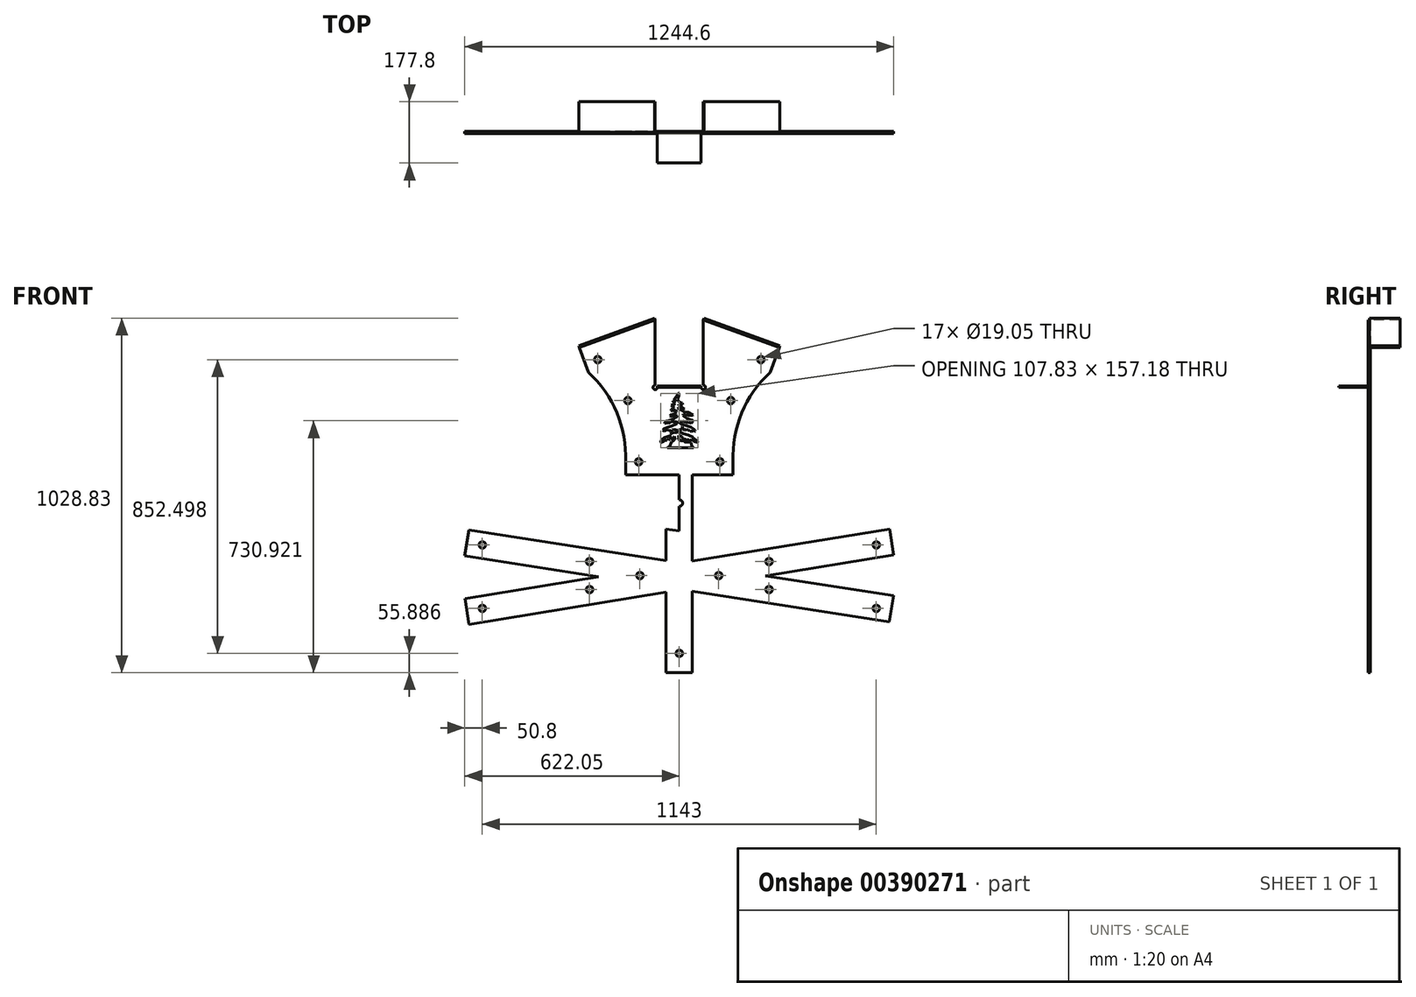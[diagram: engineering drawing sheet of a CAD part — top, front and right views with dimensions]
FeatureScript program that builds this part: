
annotation { "Feature Type Name" : "Feature", "Feature Type Description" : "" }
export const myFeature = defineFeature(function(context is Context, id is Id, definition is map)
    precondition{}
    {
        {
            var Q0;
            Q0=qCreatedBy(makeId("Front.planeOp"),FACE);
            var sketch = newSketch(context, id + "F0", { "sketchPlane" : qUnion([Q0])});
            skLineSegment(sketch, "E0.bottom", {"start": v(-203.2, 255.59) * mm, "end": v(203.2, 255.59) * mm});
            skLineSegment(sketch, "E0.left", {"start": v(-203.2, 255.59) * mm, "end": v(-203.2, -255.59) * mm});
            skLineSegment(sketch, "E0.right", {"start": v(203.2, 255.59) * mm, "end": v(203.2, -255.59) * mm});
            skPoint(sketch, "E0.middle", {"position": v(0, 0) * mm});
            skLineSegment(sketch, "E1", {"start": v(-203.2, 255.59) * mm, "end": v(0, 329.25) * mm});
            skLineSegment(sketch, "E2", {"start": v(0, 329.25) * mm, "end": v(203.2, 255.59) * mm});
            skLineSegment(sketch, "E3", {"start": v(-167.38, -1.62) * mm, "end": v(-203.2, 255.59) * mm});
            skLineSegment(sketch, "E4", {"start": v(-167.38, -1.62) * mm, "end": v(-203.2, -14.6) * mm});
            skLineSegment(sketch, "E5.top", {"start": v(-203.2, -814.39) * mm, "end": v(203.2, -814.39) * mm});
            skLineSegment(sketch, "E5.left", {"start": v(-203.2, -255.59) * mm, "end": v(-203.2, -814.39) * mm});
            skLineSegment(sketch, "E5.right", {"start": v(203.2, -255.59) * mm, "end": v(203.2, -814.39) * mm});
            skLineSegment(sketch, "E6.bottom", {"start": v(-69.85, 348.41) * mm, "end": v(69.85, 348.41) * mm});
            skLineSegment(sketch, "E6.top", {"start": v(-69.85, 113.35) * mm, "end": v(69.85, 113.35) * mm});
            skLineSegment(sketch, "E6.left", {"start": v(-69.85, 348.41) * mm, "end": v(-69.85, 113.35) * mm});
            skLineSegment(sketch, "E6.right", {"start": v(69.85, 348.41) * mm, "end": v(69.85, 113.35) * mm});
            skPoint(sketch, "E6.middle", {"position": v(0, 230.88) * mm});
            skLineSegment(sketch, "E7.top", {"start": v(-69.85, 303.93) * mm, "end": v(69.85, 303.93) * mm});
            skLineSegment(sketch, "E7.left", {"start": v(-69.85, 348.41) * mm, "end": v(-69.85, 303.93) * mm});
            skLineSegment(sketch, "E7.right", {"start": v(69.85, 348.41) * mm, "end": v(69.85, 303.93) * mm});
            skLineSegment(sketch, "E8", {"start": v(0, 329.25) * mm, "end": v(-340.45, 205.83) * mm});
            skLineSegment(sketch, "E9", {"start": v(-203.2, -14.6) * mm, "end": v(-289.77, 224.2) * mm});
            skLineSegment(sketch, "E10", {"start": v(0, 329.25) * mm, "end": v(318.78, 213.69) * mm});
            skLineSegment(sketch, "E11", {"start": v(203.2, -144.94) * mm, "end": v(-203.2, -144.94) * mm});
            skLineSegment(sketch, "E12", {"start": v(-203.2, -14.6) * mm, "end": v(-155.95, -144.94) * mm});
            skCircle(sketch, "E13", {"center": v(-236.63, 189.45) * mm, "radius": 9.53 * mm});
            skCircle(sketch, "E14", {"center": v(-149.23, 70.58) * mm, "radius": 9.53 * mm});
            skCircle(sketch, "E15", {"center": v(-117.86, -107.22) * mm, "radius": 9.53 * mm});
            skCircle(sketch, "E16", {"center": v(-100.67, -17.94) * mm, "radius": 3.18 * mm});
            skLineSegment(sketch, "E17", {"start": v(-289.77, 224.2) * mm, "end": v(-291.93, 230.18) * mm});
            skLineSegment(sketch, "E18", {"start": v(-291.93, 230.18) * mm, "end": v(-72.01, 309.9) * mm});
            skLineSegment(sketch, "E19", {"start": v(-72.01, 309.9) * mm, "end": v(-69.85, 303.93) * mm});
            skLineSegment(sketch, "E20", {"start": v(-69.85, 113.35) * mm, "end": v(-69.85, 108.57) * mm});
            skLineSegment(sketch, "E21", {"start": v(-69.85, 108.57) * mm, "end": v(69.85, 108.57) * mm});
            skLineSegment(sketch, "E22", {"start": v(69.85, 108.57) * mm, "end": v(69.85, 113.35) * mm});
            skLineSegment(sketch, "E23", {"start": v(69.85, 303.93) * mm, "end": v(72.01, 309.9) * mm});
            skLineSegment(sketch, "E24", {"start": v(72.01, 309.9) * mm, "end": v(291.93, 230.18) * mm});
            skLineSegment(sketch, "E25", {"start": v(291.93, 230.18) * mm, "end": v(289.77, 224.2) * mm});
            skLineSegment(sketch, "E26", {"start": v(-63.5, 113.35) * mm, "end": v(-63.5, 108.57) * mm});
            skLineSegment(sketch, "E27", {"start": v(63.5, 113.35) * mm, "end": v(63.5, 108.57) * mm});
            skCircle(sketch, "E28", {"center": v(-69.85, 108.57) * mm, "radius": 6.35 * mm});
            skCircle(sketch, "E29", {"center": v(69.85, 108.57) * mm, "radius": 6.35 * mm});
            skCircle(sketch, "E30", {"center": v(0, -106.84) * mm, "radius": 3.18 * mm});
            skCircle(sketch, "E31", {"center": v(117.86, -107.22) * mm, "radius": 9.53 * mm});
            skCircle(sketch, "E32", {"center": v(100.67, -17.94) * mm, "radius": 3.18 * mm});
            skCircle(sketch, "E33", {"center": v(149.22, 70.58) * mm, "radius": 9.53 * mm});
            skCircle(sketch, "E34", {"center": v(236.63, 189.45) * mm, "radius": 9.53 * mm});
            skLineSegment(sketch, "E35", {"start": v(203.2, -14.6) * mm, "end": v(167.38, -1.62) * mm});
            skLineSegment(sketch, "E36", {"start": v(167.38, -1.62) * mm, "end": v(203.2, 255.59) * mm});
            skLineSegment(sketch, "E37", {"start": v(203.2, -14.6) * mm, "end": v(289.77, 224.2) * mm});
            skLineSegment(sketch, "E38", {"start": v(203.2, -14.6) * mm, "end": v(155.95, -144.94) * mm});
            skLineSegment(sketch, "E39", {"start": v(155.95, -144.94) * mm, "end": v(155.95, -106.84) * mm});
            skLineSegment(sketch, "E40", {"start": v(-155.95, -144.94) * mm, "end": v(-155.95, -106.84) * mm});
            skArc(sketch, "E41", {"start": v(-155.95, -106.84) * mm, "mid": v(-180.99, 34.87) * mm, "end": v(-263.8, 152.57) * mm});
            skArc(sketch, "E42", {"start": v(263.8, 152.57) * mm, "mid": v(180.99, 34.87) * mm, "end": v(155.95, -106.84) * mm});
            skLineSegment(sketch, "E43", {"start": v(-30.75, -64.04) * mm, "end": v(33.83, -64.04) * mm});
            skLineSegment(sketch, "E44", {"start": v(33.83, -64.04) * mm, "end": v(33.83, -51.53) * mm});
            skLineSegment(sketch, "E45", {"start": v(33.83, -51.53) * mm, "end": v(31.7, -50.31) * mm});
            skLineSegment(sketch, "E46", {"start": v(31.7, -50.31) * mm, "end": v(13.72, -50.31) * mm});
            skLineSegment(sketch, "E47", {"start": v(16.16, -45.44) * mm, "end": v(4.28, -45.44) * mm});
            skLineSegment(sketch, "E48", {"start": v(4.28, -45.44) * mm, "end": v(-1.5, -42.09) * mm});
            skLineSegment(sketch, "E49", {"start": v(-1.5, -42.09) * mm, "end": v(-1.5, -30.2) * mm});
            skLineSegment(sketch, "E50", {"start": v(-1.5, -30.2) * mm, "end": v(0.62, -30.2) * mm});
            skLineSegment(sketch, "E51", {"start": v(0.62, -30.2) * mm, "end": v(45.98, -54.03) * mm});
            skLineSegment(sketch, "E52", {"start": v(35.59, -66.15) * mm, "end": v(45.98, -54.03) * mm});
            skLineSegment(sketch, "E53", {"start": v(35.59, -66.15) * mm, "end": v(6.07, -40.85) * mm});
            skLineSegment(sketch, "E54", {"start": v(6.07, -40.85) * mm, "end": v(6.07, -36.35) * mm});
            skLineSegment(sketch, "E55", {"start": v(6.07, -36.35) * mm, "end": v(6.76, -34.82) * mm});
            skLineSegment(sketch, "E56", {"start": v(6.76, -34.82) * mm, "end": v(9.8, -37.56) * mm});
            skLineSegment(sketch, "E57", {"start": v(9.8, -37.56) * mm, "end": v(11.02, -40.91) * mm});
            skLineSegment(sketch, "E58", {"start": v(11.02, -40.91) * mm, "end": v(11.93, -42.44) * mm});
            skLineSegment(sketch, "E59", {"start": v(11.93, -42.44) * mm, "end": v(14.07, -41.52) * mm});
            skLineSegment(sketch, "E60", {"start": v(17.72, -41.52) * mm, "end": v(18.64, -43.05) * mm});
            skLineSegment(sketch, "E61", {"start": v(18.64, -43.05) * mm, "end": v(20.46, -42.44) * mm});
            skLineSegment(sketch, "E62", {"start": v(20.46, -42.44) * mm, "end": v(22.6, -40.91) * mm});
            skLineSegment(sketch, "E63", {"start": v(22.6, -40.91) * mm, "end": v(23.5, -43.35) * mm});
            skLineSegment(sketch, "E64", {"start": v(23.5, -43.35) * mm, "end": v(23.81, -45.79) * mm});
            skLineSegment(sketch, "E65", {"start": v(23.81, -45.79) * mm, "end": v(26.25, -46.4) * mm});
            skLineSegment(sketch, "E66", {"start": v(26.25, -46.4) * mm, "end": v(27.77, -45.48) * mm});
            skLineSegment(sketch, "E67", {"start": v(27.77, -45.48) * mm, "end": v(28.69, -43.35) * mm});
            skLineSegment(sketch, "E68", {"start": v(28.69, -43.35) * mm, "end": v(29.6, -42.13) * mm});
            skLineSegment(sketch, "E69", {"start": v(29.6, -42.13) * mm, "end": v(31.12, -43.96) * mm});
            skLineSegment(sketch, "E70", {"start": v(31.12, -43.96) * mm, "end": v(33.26, -44.87) * mm});
            skLineSegment(sketch, "E71", {"start": v(33.26, -44.87) * mm, "end": v(34.78, -44.87) * mm});
            skLineSegment(sketch, "E72", {"start": v(34.78, -44.87) * mm, "end": v(37.83, -43.05) * mm});
            skLineSegment(sketch, "E73", {"start": v(37.83, -43.05) * mm, "end": v(39.35, -43.66) * mm});
            skLineSegment(sketch, "E74", {"start": v(39.35, -43.66) * mm, "end": v(43.61, -47.92) * mm});
            skLineSegment(sketch, "E75", {"start": v(43.61, -47.92) * mm, "end": v(49.4, -50.05) * mm});
            skLineSegment(sketch, "E76", {"start": v(49.4, -50.05) * mm, "end": v(52.75, -49.44) * mm});
            skLineSegment(sketch, "E77", {"start": v(52.75, -49.44) * mm, "end": v(53.67, -46.7) * mm});
            skLineSegment(sketch, "E78", {"start": v(53.67, -46.7) * mm, "end": v(50.32, -44.27) * mm});
            skLineSegment(sketch, "E79", {"start": v(50.32, -44.27) * mm, "end": v(41.18, -41.52) * mm});
            skLineSegment(sketch, "E80", {"start": v(41.18, -41.52) * mm, "end": v(37.83, -39.09) * mm});
            skLineSegment(sketch, "E81", {"start": v(37.83, -39.09) * mm, "end": v(39.96, -37.87) * mm});
            skLineSegment(sketch, "E82", {"start": v(39.96, -37.87) * mm, "end": v(40.57, -35.74) * mm});
            skLineSegment(sketch, "E83", {"start": v(40.57, -35.74) * mm, "end": v(25.95, -29.64) * mm});
            skLineSegment(sketch, "E84", {"start": v(25.95, -29.64) * mm, "end": v(11.63, -25.38) * mm});
            skLineSegment(sketch, "E85", {"start": v(11.63, -25.38) * mm, "end": v(4.01, -22.33) * mm});
            skLineSegment(sketch, "E86", {"start": v(4.01, -22.33) * mm, "end": v(1.88, -21.42) * mm});
            skLineSegment(sketch, "E87", {"start": v(1.88, -21.42) * mm, "end": v(0.97, -14.72) * mm});
            skLineSegment(sketch, "E88", {"start": v(0.97, -14.72) * mm, "end": v(1.58, -11.67) * mm});
            skLineSegment(sketch, "E89", {"start": v(1.58, -11.67) * mm, "end": v(1.88, -9.84) * mm});
            skLineSegment(sketch, "E90", {"start": v(1.88, -9.84) * mm, "end": v(4.01, -13.5) * mm});
            skLineSegment(sketch, "E91", {"start": v(4.01, -13.5) * mm, "end": v(6.76, -13.5) * mm});
            skLineSegment(sketch, "E92", {"start": v(6.76, -13.5) * mm, "end": v(7.97, -10.76) * mm});
            skLineSegment(sketch, "E93", {"start": v(7.97, -10.76) * mm, "end": v(5.84, -7.71) * mm});
            skLineSegment(sketch, "E94", {"start": v(5.84, -7.71) * mm, "end": v(7.97, -6.8) * mm});
            skLineSegment(sketch, "E95", {"start": v(7.97, -6.8) * mm, "end": v(11.02, -9.54) * mm});
            skLineSegment(sketch, "E96", {"start": v(11.02, -9.54) * mm, "end": v(10.72, -12.9) * mm});
            skLineSegment(sketch, "E97", {"start": v(10.72, -12.9) * mm, "end": v(11.93, -14.1) * mm});
            skLineSegment(sketch, "E98", {"start": v(11.93, -14.1) * mm, "end": v(14.07, -13.8) * mm});
            skLineSegment(sketch, "E99", {"start": v(14.07, -13.8) * mm, "end": v(14.37, -11.06) * mm});
            skLineSegment(sketch, "E100", {"start": v(14.37, -11.06) * mm, "end": v(15.9, -10.76) * mm});
            skLineSegment(sketch, "E101", {"start": v(15.9, -10.76) * mm, "end": v(17.42, -14.72) * mm});
            skLineSegment(sketch, "E102", {"start": v(17.42, -14.72) * mm, "end": v(20.46, -15.02) * mm});
            skLineSegment(sketch, "E103", {"start": v(20.46, -15.02) * mm, "end": v(21.68, -14.1) * mm});
            skLineSegment(sketch, "E104", {"start": v(21.68, -14.1) * mm, "end": v(21.99, -12.59) * mm});
            skLineSegment(sketch, "E105", {"start": v(21.99, -12.59) * mm, "end": v(25.34, -14.41) * mm});
            skLineSegment(sketch, "E106", {"start": v(25.34, -14.41) * mm, "end": v(25.34, -16.24) * mm});
            skLineSegment(sketch, "E107", {"start": v(25.34, -16.24) * mm, "end": v(30.82, -15.94) * mm});
            skLineSegment(sketch, "E108", {"start": v(30.82, -15.94) * mm, "end": v(32.65, -17.76) * mm});
            skLineSegment(sketch, "E109", {"start": v(32.65, -17.76) * mm, "end": v(35.39, -18.98) * mm});
            skLineSegment(sketch, "E110", {"start": v(36.6, -14.41) * mm, "end": v(39.96, -17.16) * mm});
            skLineSegment(sketch, "E111", {"start": v(39.96, -17.16) * mm, "end": v(43.92, -19.6) * mm});
            skLineSegment(sketch, "E112", {"start": v(43.92, -19.6) * mm, "end": v(45.75, -18.37) * mm});
            skLineSegment(sketch, "E113", {"start": v(45.75, -18.37) * mm, "end": v(45.14, -15.02) * mm});
            skLineSegment(sketch, "E114", {"start": v(45.14, -15.02) * mm, "end": v(40.87, -11.06) * mm});
            skLineSegment(sketch, "E115", {"start": v(40.87, -11.06) * mm, "end": v(33.26, -6.8) * mm});
            skLineSegment(sketch, "E116", {"start": v(33.26, -6.8) * mm, "end": v(21.99, -3.14) * mm});
            skLineSegment(sketch, "E117", {"start": v(21.99, -3.14) * mm, "end": v(10.1, 0.82) * mm});
            skLineSegment(sketch, "E118", {"start": v(10.1, 0.82) * mm, "end": v(3.1, 4.47) * mm});
            skLineSegment(sketch, "E119", {"start": v(3.1, 4.47) * mm, "end": v(1.27, 7.21) * mm});
            skLineSegment(sketch, "E120", {"start": v(1.27, 7.21) * mm, "end": v(3.1, 9.04) * mm});
            skLineSegment(sketch, "E121", {"start": v(3.1, 9.04) * mm, "end": v(5.54, 6.9) * mm});
            skLineSegment(sketch, "E122", {"start": v(5.54, 6.9) * mm, "end": v(9.5, 6.9) * mm});
            skLineSegment(sketch, "E123", {"start": v(9.5, 6.9) * mm, "end": v(9.8, 9.04) * mm});
            skLineSegment(sketch, "E124", {"start": v(9.8, 9.04) * mm, "end": v(10.72, 10.87) * mm});
            skLineSegment(sketch, "E125", {"start": v(10.72, 10.87) * mm, "end": v(16.5, 8.13) * mm});
            skLineSegment(sketch, "E126", {"start": v(16.5, 8.13) * mm, "end": v(20.46, 6.9) * mm});
            skLineSegment(sketch, "E127", {"start": v(20.46, 6.9) * mm, "end": v(23.81, 6) * mm});
            skLineSegment(sketch, "E128", {"start": v(23.81, 6) * mm, "end": v(27.47, 6.9) * mm});
            skLineSegment(sketch, "E129", {"start": v(27.47, 6.9) * mm, "end": v(30.52, 6) * mm});
            skLineSegment(sketch, "E130", {"start": v(30.52, 6) * mm, "end": v(35.08, 5.08) * mm});
            skLineSegment(sketch, "E131", {"start": v(35.08, 5.08) * mm, "end": v(40.18, 11.54) * mm});
            skLineSegment(sketch, "E132", {"start": v(40.18, 11.54) * mm, "end": v(37.74, 13.98) * mm});
            skLineSegment(sketch, "E133", {"start": v(37.74, 13.98) * mm, "end": v(32.87, 14.9) * mm});
            skLineSegment(sketch, "E134", {"start": v(32.87, 14.9) * mm, "end": v(22.82, 18.24) * mm});
            skLineSegment(sketch, "E135", {"start": v(22.82, 18.24) * mm, "end": v(15.2, 23.72) * mm});
            skLineSegment(sketch, "E136", {"start": v(15.2, 23.72) * mm, "end": v(10.94, 28.3) * mm});
            skLineSegment(sketch, "E137", {"start": v(10.94, 28.3) * mm, "end": v(11.85, 31.04) * mm});
            skLineSegment(sketch, "E138", {"start": v(11.85, 31.04) * mm, "end": v(13.98, 31.95) * mm});
            skLineSegment(sketch, "E139", {"start": v(13.98, 31.95) * mm, "end": v(17.34, 29.51) * mm});
            skLineSegment(sketch, "E140", {"start": v(17.34, 29.51) * mm, "end": v(25.26, 27.38) * mm});
            skLineSegment(sketch, "E141", {"start": v(25.26, 27.38) * mm, "end": v(33.48, 27.38) * mm});
            skLineSegment(sketch, "E142", {"start": v(33.48, 27.38) * mm, "end": v(39.27, 27.08) * mm});
            skLineSegment(sketch, "E143", {"start": v(39.27, 27.08) * mm, "end": v(40.49, 29.2) * mm});
            skLineSegment(sketch, "E144", {"start": v(40.49, 29.2) * mm, "end": v(26.28, 36.36) * mm});
            skLineSegment(sketch, "E145", {"start": v(26.28, 36.36) * mm, "end": v(20.49, 36.66) * mm});
            skLineSegment(sketch, "E146", {"start": v(20.49, 36.66) * mm, "end": v(13.18, 37.27) * mm});
            skLineSegment(sketch, "E147", {"start": v(13.18, 37.27) * mm, "end": v(8, 41.54) * mm});
            skLineSegment(sketch, "E148", {"start": v(8, 41.54) * mm, "end": v(3.12, 44.58) * mm});
            skLineSegment(sketch, "E149", {"start": v(3.12, 44.58) * mm, "end": v(-3.27, 48.24) * mm});
            skLineSegment(sketch, "E150", {"start": v(-3.27, 48.24) * mm, "end": v(-3.27, 50.07) * mm});
            skLineSegment(sketch, "E151", {"start": v(-1.14, 50.37) * mm, "end": v(4.04, 47.02) * mm});
            skLineSegment(sketch, "E152", {"start": v(4.04, 47.02) * mm, "end": v(8.3, 44.89) * mm});
            skLineSegment(sketch, "E153", {"start": v(8.3, 44.89) * mm, "end": v(13.18, 44.89) * mm});
            skLineSegment(sketch, "E154", {"start": v(13.18, 44.89) * mm, "end": v(14.7, 46.41) * mm});
            skLineSegment(sketch, "E155", {"start": v(14.7, 46.41) * mm, "end": v(10.74, 49.76) * mm});
            skLineSegment(sketch, "E156", {"start": v(10.74, 49.76) * mm, "end": v(3.43, 54.33) * mm});
            skLineSegment(sketch, "E157", {"start": v(3.43, 54.33) * mm, "end": v(-1.44, 57.07) * mm});
            skLineSegment(sketch, "E158", {"start": v(-1.44, 57.07) * mm, "end": v(-1.44, 59.51) * mm});
            skLineSegment(sketch, "E159", {"start": v(-1.44, 59.51) * mm, "end": v(5.26, 59.2) * mm});
            skLineSegment(sketch, "E160", {"start": v(5.26, 59.2) * mm, "end": v(9.22, 58.9) * mm});
            skLineSegment(sketch, "E161", {"start": v(9.22, 58.9) * mm, "end": v(10.13, 60.73) * mm});
            skLineSegment(sketch, "E162", {"start": v(10.13, 60.73) * mm, "end": v(7.7, 63.78) * mm});
            skLineSegment(sketch, "E163", {"start": v(7.7, 63.78) * mm, "end": v(1.6, 65.9) * mm});
            skLineSegment(sketch, "E164", {"start": v(1.6, 65.9) * mm, "end": v(-3.27, 68.04) * mm});
            skLineSegment(sketch, "E165", {"start": v(-3.27, 68.04) * mm, "end": v(-3.88, 74.13) * mm});
            skLineSegment(sketch, "E166", {"start": v(-3.88, 74.13) * mm, "end": v(-2.66, 79.31) * mm});
            skLineSegment(sketch, "E167", {"start": v(-2.66, 79.31) * mm, "end": v(-0.84, 87.53) * mm});
            skLineSegment(sketch, "E168", {"start": v(-0.84, 87.53) * mm, "end": v(-2.05, 90.58) * mm});
            skLineSegment(sketch, "E169", {"start": v(-2.05, 90.58) * mm, "end": v(-4.19, 90.58) * mm});
            skLineSegment(sketch, "E170", {"start": v(-4.19, 90.58) * mm, "end": v(-6.32, 88.75) * mm});
            skLineSegment(sketch, "E171", {"start": v(-6.32, 88.75) * mm, "end": v(-6.62, 83.88) * mm});
            skLineSegment(sketch, "E172", {"start": v(-6.62, 83.88) * mm, "end": v(-10.58, 79.92) * mm});
            skLineSegment(sketch, "E173", {"start": v(-10.58, 79.92) * mm, "end": v(-13.93, 76.57) * mm});
            skLineSegment(sketch, "E174", {"start": v(-13.93, 76.57) * mm, "end": v(-16.07, 73.83) * mm});
            skLineSegment(sketch, "E175", {"start": v(-16.07, 73.83) * mm, "end": v(-13.63, 72.6) * mm});
            skLineSegment(sketch, "E176", {"start": v(-13.63, 72.6) * mm, "end": v(-9.67, 73.22) * mm});
            skLineSegment(sketch, "E177", {"start": v(-9.67, 73.22) * mm, "end": v(-10.89, 71.09) * mm});
            skLineSegment(sketch, "E178", {"start": v(-10.89, 71.09) * mm, "end": v(-14.85, 70.17) * mm});
            skLineSegment(sketch, "E179", {"start": v(-14.85, 70.17) * mm, "end": v(-18.5, 69.26) * mm});
            skLineSegment(sketch, "E180", {"start": v(-18.5, 69.26) * mm, "end": v(-18.2, 67.13) * mm});
            skLineSegment(sketch, "E181", {"start": v(-18.2, 67.13) * mm, "end": v(-14.85, 65) * mm});
            skLineSegment(sketch, "E182", {"start": v(-14.85, 65) * mm, "end": v(-11.8, 62.25) * mm});
            skLineSegment(sketch, "E183", {"start": v(-11.8, 62.25) * mm, "end": v(-15.15, 59.2) * mm});
            skLineSegment(sketch, "E184", {"start": v(-15.15, 59.2) * mm, "end": v(-21.55, 58.6) * mm});
            skLineSegment(sketch, "E185", {"start": v(-21.55, 58.6) * mm, "end": v(-23.04, 57.1) * mm});
            skLineSegment(sketch, "E186", {"start": v(-23.04, 57.1) * mm, "end": v(-10.3, 44.38) * mm});
            skLineSegment(sketch, "E187", {"start": v(-10.3, 44.38) * mm, "end": v(-5.73, 42.55) * mm});
            skLineSegment(sketch, "E188", {"start": v(-5.73, 42.55) * mm, "end": v(-0.86, 43.77) * mm});
            skLineSegment(sketch, "E189", {"start": v(-0.86, 43.77) * mm, "end": v(-0.25, 41.94) * mm});
            skLineSegment(sketch, "E190", {"start": v(-0.25, 41.94) * mm, "end": v(-3, 40.42) * mm});
            skLineSegment(sketch, "E191", {"start": v(-3, 40.42) * mm, "end": v(-3, 36.46) * mm});
            skLineSegment(sketch, "E192", {"start": v(-3, 36.46) * mm, "end": v(-8.78, 36.15) * mm});
            skLineSegment(sketch, "E193", {"start": v(-8.78, 36.15) * mm, "end": v(-13.65, 32.8) * mm});
            skLineSegment(sketch, "E194", {"start": v(-13.65, 32.8) * mm, "end": v(-19.75, 30.06) * mm});
            skLineSegment(sketch, "E195", {"start": v(-19.75, 30.06) * mm, "end": v(-24.62, 28.84) * mm});
            skLineSegment(sketch, "E196", {"start": v(-24.62, 28.84) * mm, "end": v(-26.75, 27.01) * mm});
            skLineSegment(sketch, "E197", {"start": v(-26.75, 27.01) * mm, "end": v(-25.23, 24.58) * mm});
            skLineSegment(sketch, "E198", {"start": v(-25.23, 24.58) * mm, "end": v(-19.75, 24.27) * mm});
            skLineSegment(sketch, "E199", {"start": v(-19.75, 24.27) * mm, "end": v(-13.04, 26.4) * mm});
            skLineSegment(sketch, "E200", {"start": v(-13.04, 26.4) * mm, "end": v(-10.3, 27.01) * mm});
            skLineSegment(sketch, "E201", {"start": v(-10.3, 27.01) * mm, "end": v(-6.34, 26.7) * mm});
            skLineSegment(sketch, "E202", {"start": v(-6.34, 26.7) * mm, "end": v(-5.73, 24.88) * mm});
            skLineSegment(sketch, "E203", {"start": v(-5.73, 24.88) * mm, "end": v(-8.17, 22.44) * mm});
            skLineSegment(sketch, "E204", {"start": v(-8.17, 22.44) * mm, "end": v(-12.13, 20.92) * mm});
            skLineSegment(sketch, "E205", {"start": v(-12.13, 20.92) * mm, "end": v(-16.1, 16.96) * mm});
            skLineSegment(sketch, "E206", {"start": v(-16.1, 16.96) * mm, "end": v(-27.67, 13.61) * mm});
            skLineSegment(sketch, "E207", {"start": v(-27.67, 13.61) * mm, "end": v(-36.2, 11.17) * mm});
            skLineSegment(sketch, "E208", {"start": v(-36.2, 11.17) * mm, "end": v(-42.6, 7.82) * mm});
            skLineSegment(sketch, "E209", {"start": v(-42.6, 7.82) * mm, "end": v(-42.9, 5.39) * mm});
            skLineSegment(sketch, "E210", {"start": v(-42.9, 5.39) * mm, "end": v(-40.15, 4.47) * mm});
            skLineSegment(sketch, "E211", {"start": v(-40.15, 4.47) * mm, "end": v(-37.72, 5.7) * mm});
            skLineSegment(sketch, "E212", {"start": v(-37.72, 5.7) * mm, "end": v(-32.23, 5.39) * mm});
            skLineSegment(sketch, "E213", {"start": v(-32.23, 5.39) * mm, "end": v(-25.53, 8.74) * mm});
            skLineSegment(sketch, "E214", {"start": v(-25.53, 8.74) * mm, "end": v(-21.27, 10.26) * mm});
            skLineSegment(sketch, "E215", {"start": v(-21.27, 10.26) * mm, "end": v(-17, 8.13) * mm});
            skLineSegment(sketch, "E216", {"start": v(-17, 8.13) * mm, "end": v(-12.13, 8.43) * mm});
            skLineSegment(sketch, "E217", {"start": v(-12.13, 8.43) * mm, "end": v(-8.47, 9.96) * mm});
            skLineSegment(sketch, "E218", {"start": v(-8.47, 9.96) * mm, "end": v(-6.95, 10.56) * mm});
            skLineSegment(sketch, "E219", {"start": v(-6.95, 10.56) * mm, "end": v(-5.73, 6.6) * mm});
            skLineSegment(sketch, "E220", {"start": v(-5.73, 6.6) * mm, "end": v(-5.43, 3.56) * mm});
            skLineSegment(sketch, "E221", {"start": v(-5.43, 3.56) * mm, "end": v(-8.47, 2.95) * mm});
            skLineSegment(sketch, "E222", {"start": v(-8.47, 2.95) * mm, "end": v(-9.39, 1.73) * mm});
            skLineSegment(sketch, "E223", {"start": v(-9.39, 1.73) * mm, "end": v(-20.66, -2.84) * mm});
            skLineSegment(sketch, "E224", {"start": v(-20.66, -2.84) * mm, "end": v(-35.89, -8.02) * mm});
            skLineSegment(sketch, "E225", {"start": v(-35.89, -8.02) * mm, "end": v(-45.03, -12.28) * mm});
            skLineSegment(sketch, "E226", {"start": v(-45.03, -12.28) * mm, "end": v(-48.07, -15.02) * mm});
            skLineSegment(sketch, "E227", {"start": v(-48.07, -15.02) * mm, "end": v(-46.86, -16.55) * mm});
            skLineSegment(sketch, "E228", {"start": v(-46.86, -16.55) * mm, "end": v(-43.2, -18.07) * mm});
            skLineSegment(sketch, "E229", {"start": v(-43.2, -18.07) * mm, "end": v(-36.5, -14.72) * mm});
            skLineSegment(sketch, "E230", {"start": v(-36.5, -14.72) * mm, "end": v(-33.45, -14.41) * mm});
            skLineSegment(sketch, "E231", {"start": v(-33.45, -14.41) * mm, "end": v(-30.1, -17.16) * mm});
            skLineSegment(sketch, "E232", {"start": v(-30.1, -17.16) * mm, "end": v(-25.84, -16.85) * mm});
            skLineSegment(sketch, "E233", {"start": v(-25.84, -16.85) * mm, "end": v(-23.4, -17.76) * mm});
            skLineSegment(sketch, "E234", {"start": v(-23.4, -17.76) * mm, "end": v(-20.66, -19.6) * mm});
            skLineSegment(sketch, "E235", {"start": v(-20.66, -19.6) * mm, "end": v(-18.22, -18.07) * mm});
            skLineSegment(sketch, "E236", {"start": v(-18.22, -18.07) * mm, "end": v(-19.44, -13.2) * mm});
            skLineSegment(sketch, "E237", {"start": v(-14.87, -14.41) * mm, "end": v(-10.3, -14.41) * mm});
            skLineSegment(sketch, "E238", {"start": v(-10.3, -14.41) * mm, "end": v(-6.34, -15.02) * mm});
            skLineSegment(sketch, "E239", {"start": v(-6.34, -15.02) * mm, "end": v(-5.12, -18.37) * mm});
            skLineSegment(sketch, "E240", {"start": v(-5.12, -18.37) * mm, "end": v(-5.12, -21.72) * mm});
            skLineSegment(sketch, "E241", {"start": v(-5.12, -21.72) * mm, "end": v(-6.95, -22.64) * mm});
            skLineSegment(sketch, "E242", {"start": v(-6.95, -22.64) * mm, "end": v(-13.35, -22.33) * mm});
            skLineSegment(sketch, "E243", {"start": v(-13.35, -22.33) * mm, "end": v(-18.53, -22.94) * mm});
            skLineSegment(sketch, "E244", {"start": v(-18.53, -22.94) * mm, "end": v(-23.7, -24.16) * mm});
            skLineSegment(sketch, "E245", {"start": v(-23.7, -24.16) * mm, "end": v(-26.14, -26.3) * mm});
            skLineSegment(sketch, "E246", {"start": v(-26.14, -26.3) * mm, "end": v(-24.62, -29.04) * mm});
            skLineSegment(sketch, "E247", {"start": v(-24.62, -29.04) * mm, "end": v(-23.4, -30.56) * mm});
            skLineSegment(sketch, "E248", {"start": v(-23.4, -30.56) * mm, "end": v(-32.54, -32.7) * mm});
            skLineSegment(sketch, "E249", {"start": v(-32.54, -32.7) * mm, "end": v(-44.42, -36.95) * mm});
            skLineSegment(sketch, "E250", {"start": v(-44.42, -36.95) * mm, "end": v(-51.42, -42.44) * mm});
            skLineSegment(sketch, "E251", {"start": v(-51.42, -42.44) * mm, "end": v(-53.56, -45.48) * mm});
            skLineSegment(sketch, "E252", {"start": v(-53.56, -45.48) * mm, "end": v(-54.17, -48.53) * mm});
            skLineSegment(sketch, "E253", {"start": v(-54.17, -48.53) * mm, "end": v(-53.25, -51.27) * mm});
            skLineSegment(sketch, "E254", {"start": v(-53.25, -51.27) * mm, "end": v(-46.86, -48.23) * mm});
            skLineSegment(sketch, "E255", {"start": v(-46.86, -48.23) * mm, "end": v(-44.11, -44.57) * mm});
            skLineSegment(sketch, "E256", {"start": v(-44.11, -44.57) * mm, "end": v(-40.15, -44.27) * mm});
            skLineSegment(sketch, "E257", {"start": v(-40.15, -44.27) * mm, "end": v(-36.2, -44.57) * mm});
            skLineSegment(sketch, "E258", {"start": v(-36.2, -44.57) * mm, "end": v(-34.67, -40.91) * mm});
            skLineSegment(sketch, "E259", {"start": v(-34.67, -40.91) * mm, "end": v(-32.23, -39.7) * mm});
            skLineSegment(sketch, "E260", {"start": v(-32.23, -39.7) * mm, "end": v(-31.63, -41.52) * mm});
            skLineSegment(sketch, "E261", {"start": v(-31.63, -41.52) * mm, "end": v(-29.5, -43.66) * mm});
            skLineSegment(sketch, "E262", {"start": v(-29.5, -43.66) * mm, "end": v(-27.06, -42.74) * mm});
            skLineSegment(sketch, "E263", {"start": v(-27.06, -42.74) * mm, "end": v(-25.84, -38.48) * mm});
            skLineSegment(sketch, "E264", {"start": v(-25.84, -38.48) * mm, "end": v(-24.62, -36.35) * mm});
            skLineSegment(sketch, "E265", {"start": v(-23.1, -38.78) * mm, "end": v(-22.8, -40.91) * mm});
            skLineSegment(sketch, "E266", {"start": v(-22.8, -40.91) * mm, "end": v(-19.44, -40.3) * mm});
            skLineSegment(sketch, "E267", {"start": v(-19.44, -40.3) * mm, "end": v(-18.22, -38.17) * mm});
            skLineSegment(sketch, "E268", {"start": v(-18.22, -38.17) * mm, "end": v(-17, -36.65) * mm});
            skLineSegment(sketch, "E269", {"start": v(-17, -36.65) * mm, "end": v(-15.79, -34.82) * mm});
            skLineSegment(sketch, "E270", {"start": v(-15.79, -34.82) * mm, "end": v(-14.26, -33.3) * mm});
            skLineSegment(sketch, "E271", {"start": v(-14.26, -33.3) * mm, "end": v(-13.96, -37.56) * mm});
            skLineSegment(sketch, "E272", {"start": v(-13.96, -37.56) * mm, "end": v(-11.52, -38.48) * mm});
            skLineSegment(sketch, "E273", {"start": v(-11.52, -38.48) * mm, "end": v(-8.78, -38.48) * mm});
            skLineSegment(sketch, "E274", {"start": v(-8.78, -38.48) * mm, "end": v(-5.73, -34.52) * mm});
            skLineSegment(sketch, "E275", {"start": v(-8.51, -29.3) * mm, "end": v(-8.82, -35.7) * mm});
            skLineSegment(sketch, "E276", {"start": v(-8.82, -35.7) * mm, "end": v(-10.04, -38.43) * mm});
            skLineSegment(sketch, "E277", {"start": v(-10.04, -38.43) * mm, "end": v(-13.08, -40.56) * mm});
            skLineSegment(sketch, "E278", {"start": v(-13.08, -40.56) * mm, "end": v(-14.91, -43.92) * mm});
            skLineSegment(sketch, "E279", {"start": v(-14.91, -43.92) * mm, "end": v(-17.04, -46.35) * mm});
            skLineSegment(sketch, "E280", {"start": v(-17.04, -46.35) * mm, "end": v(-21.61, -48.79) * mm});
            skLineSegment(sketch, "E281", {"start": v(-21.61, -48.79) * mm, "end": v(-23.74, -50.62) * mm});
            skLineSegment(sketch, "E282", {"start": v(-23.74, -50.62) * mm, "end": v(-27.1, -61.44) * mm});
            skLineSegment(sketch, "E283", {"start": v(-27.1, -61.44) * mm, "end": v(-31.05, -63.87) * mm});
            skLineSegment(sketch, "E284", {"start": v(-14.87, -14.41) * mm, "end": v(-17.99, -11.35) * mm});
            skLineSegment(sketch, "E285", {"start": v(-17.99, -11.35) * mm, "end": v(-19.47, -13.03) * mm});
            skLineSegment(sketch, "E286", {"start": v(-23.1, -38.78) * mm, "end": v(-23.1, -35.95) * mm});
            skLineSegment(sketch, "E287", {"start": v(-23.1, -35.95) * mm, "end": v(-24.6, -36.23) * mm});
            skLineSegment(sketch, "E288", {"start": v(-5.73, -34.52) * mm, "end": v(-8.51, -29.3) * mm});
            skLineSegment(sketch, "E289", {"start": v(14.17, -41.37) * mm, "end": v(17.72, -41.52) * mm});
            skLineSegment(sketch, "E290", {"start": v(16.16, -45.44) * mm, "end": v(17.36, -47.06) * mm});
            skLineSegment(sketch, "E291", {"start": v(17.36, -47.06) * mm, "end": v(15.5, -48.17) * mm});
            skLineSegment(sketch, "E292", {"start": v(15.5, -48.17) * mm, "end": v(13.9, -50.15) * mm});
            skLineSegment(sketch, "E293", {"start": v(-31.05, -63.87) * mm, "end": v(-30.75, -64.04) * mm});
            skLineSegment(sketch, "E294", {"start": v(35.39, -18.98) * mm, "end": v(37.1, -17.74) * mm});
            skLineSegment(sketch, "E295", {"start": v(37.1, -17.74) * mm, "end": v(36.63, -14.4) * mm});
            skLineSegment(sketch, "E296", {"start": v(-3.27, 50.07) * mm, "end": v(-1.14, 50.37) * mm});
            skLineSegment(sketch, "E297", {"start": v(-5.73, 6.6) * mm, "end": v(1.27, 7.21) * mm});
            skLineSegment(sketch, "E298", {"start": v(-8.51, -29.3) * mm, "end": v(-1.5, -30.2) * mm});
            skLineSegment(sketch, "E299", {"start": v(-5.12, -18.37) * mm, "end": v(0.97, -14.72) * mm});
            skLineSegment(sketch, "E300", {"start": v(-20.66, -2.84) * mm, "end": v(33.26, -6.8) * mm});
            skLineSegment(sketch, "E301", {"start": v(15.9, -10.76) * mm, "end": v(33.26, -6.8) * mm});
            skLineSegment(sketch, "E302", {"start": v(-17.99, -11.35) * mm, "end": v(-20.66, -2.84) * mm});
            skLineSegment(sketch, "E303", {"start": v(-19.47, -13.03) * mm, "end": v(-19.44, -13.2) * mm});
            skLineSegment(sketch, "E304", {"start": v(37.83, -39.09) * mm, "end": v(37.83, -43.05) * mm});
            skLineSegment(sketch, "E305", {"start": v(11.63, -25.38) * mm, "end": v(6.76, -34.82) * mm});
            skLineSegment(sketch, "E306", {"start": v(-23.1, -35.95) * mm, "end": v(-23.4, -30.56) * mm});
            skLineSegment(sketch, "E307", {"start": v(-5.72, -34.48) * mm, "end": v(-6.95, -22.64) * mm});
            skLineSegment(sketch, "E308", {"start": v(22.6, -40.91) * mm, "end": v(25.95, -29.64) * mm});
            skLineSegment(sketch, "E309", {"start": v(-44.42, -36.95) * mm, "end": v(-36.2, -44.57) * mm});
            skLineSegment(sketch, "E310", {"start": v(-24.6, -36.23) * mm, "end": v(-24.62, -36.35) * mm});
            skLineSegment(sketch, "E311", {"start": v(14.07, -41.52) * mm, "end": v(14.17, -41.37) * mm});
            skLineSegment(sketch, "E312", {"start": v(13.72, -50.31) * mm, "end": v(13.9, -50.15) * mm});
            skLineSegment(sketch, "E313", {"start": v(39.96, -37.87) * mm, "end": v(42.96, -39.8) * mm});
            skLineSegment(sketch, "E314", {"start": v(42.96, -39.8) * mm, "end": v(50.29, -44.1) * mm});
            skLineSegment(sketch, "E315", {"start": v(50.32, -44.27) * mm, "end": v(50.29, -44.1) * mm});
            skLineSegment(sketch, "E316", {"start": v(33.83, -64.04) * mm, "end": v(33.83, -66.54) * mm});
            skLineSegment(sketch, "E317", {"start": v(33.83, -66.54) * mm, "end": v(-34.74, -66.54) * mm});
            skLineSegment(sketch, "E318", {"start": v(-34.74, -66.54) * mm, "end": v(-31.05, -63.87) * mm});
            skLineSegment(sketch, "E319", {"start": v(203.2, -576.09) * mm, "end": v(291.12, -589.8) * mm});
            skLineSegment(sketch, "E320", {"start": v(291.12, -589.27) * mm, "end": v(291.12, -589.8) * mm});
            skLineSegment(sketch, "E321", {"start": v(-203.2, -579.8) * mm, "end": v(-290.93, -594.2) * mm});
            skLineSegment(sketch, "E322", {"start": v(-290.93, -594.2) * mm, "end": v(-291.09, -593.18) * mm});
            skLineSegment(sketch, "E323", {"start": v(437.2, -240.73) * mm, "end": v(-703.05, -427.97) * mm});
            skLineSegment(sketch, "E324", {"start": v(-683.8, -680.87) * mm, "end": v(506.1, -485.48) * mm});
            skLineSegment(sketch, "E325", {"start": v(525.09, -649.6) * mm, "end": v(-857.76, -435.44) * mm});
            skLineSegment(sketch, "E326", {"start": v(-603.53, -214.61) * mm, "end": v(936.97, -453.19) * mm});
            skLineSegment(sketch, "E327.bottom", {"start": v(-38.1, -144.94) * mm, "end": v(38.1, -144.94) * mm});
            skLineSegment(sketch, "E327.top", {"start": v(-38.1, -718.93) * mm, "end": v(38.1, -718.93) * mm});
            skLineSegment(sketch, "E327.left", {"start": v(-38.1, -144.94) * mm, "end": v(-38.1, -718.93) * mm});
            skLineSegment(sketch, "E327.right", {"start": v(38.1, -144.94) * mm, "end": v(38.1, -718.93) * mm});
            skLineSegment(sketch, "E328", {"start": v(446.8, -328.68) * mm, "end": v(-636.39, -506.54) * mm});
            skLineSegment(sketch, "E329", {"start": v(-621.95, -581.4) * mm, "end": v(535.16, -391.39) * mm});
            skLineSegment(sketch, "E330", {"start": v(550.05, -561.96) * mm, "end": v(-596.62, -384.38) * mm});
            skLineSegment(sketch, "E331", {"start": v(-586.91, -308.77) * mm, "end": v(562.27, -486.75) * mm});
            skLineSegment(sketch, "E332", {"start": v(-621.95, -504.17) * mm, "end": v(-609.6, -579.36) * mm});
            skLineSegment(sketch, "E333", {"start": v(-596.62, -384.38) * mm, "end": v(-737.65, -362.54) * mm});
            skLineSegment(sketch, "E334", {"start": v(-586.91, -308.77) * mm, "end": v(-721.28, -287.97) * mm});
            skLineSegment(sketch, "E335", {"start": v(-622.3, -380.4) * mm, "end": v(-610.64, -305.1) * mm});
            skLineSegment(sketch, "E336", {"start": v(-621.95, -581.4) * mm, "end": v(-707.9, -595.5) * mm});
            skLineSegment(sketch, "E337", {"start": v(-636.39, -506.54) * mm, "end": v(-716.2, -519.65) * mm});
            skLineSegment(sketch, "E338", {"start": v(446.8, -328.68) * mm, "end": v(668.6, -292.26) * mm});
            skLineSegment(sketch, "E339", {"start": v(535.16, -391.39) * mm, "end": v(709.44, -362.77) * mm});
            skLineSegment(sketch, "E340", {"start": v(562.27, -486.75) * mm, "end": v(715.76, -510.52) * mm});
            skLineSegment(sketch, "E341", {"start": v(550.05, -561.96) * mm, "end": v(703.47, -585.72) * mm});
            skLineSegment(sketch, "E342", {"start": v(609.6, -571.18) * mm, "end": v(621.26, -495.88) * mm});
            skLineSegment(sketch, "E343", {"start": v(622.3, -377.08) * mm, "end": v(609.95, -301.89) * mm});
            skCircle(sketch, "E344", {"center": v(0, -226.89) * mm, "radius": 9.53 * mm});
            skCircle(sketch, "E345", {"center": v(-114.3, -437.42) * mm, "radius": 9.53 * mm});
            skCircle(sketch, "E346", {"center": v(114.3, -437.42) * mm, "radius": 9.53 * mm});
            skCircle(sketch, "E347", {"center": v(0, -663.04) * mm, "radius": 9.53 * mm});
            skCircle(sketch, "E348", {"center": v(260.35, -478.06) * mm, "radius": 9.53 * mm});
            skCircle(sketch, "E349", {"center": v(260.35, -396.78) * mm, "radius": 9.53 * mm});
            skCircle(sketch, "E350", {"center": v(571.5, -532.67) * mm, "radius": 9.53 * mm});
            skCircle(sketch, "E351", {"center": v(571.5, -348.52) * mm, "radius": 9.53 * mm});
            skCircle(sketch, "E352", {"center": v(-260.35, -478.06) * mm, "radius": 9.53 * mm});
            skCircle(sketch, "E353", {"center": v(-260.35, -396.78) * mm, "radius": 9.53 * mm});
            skCircle(sketch, "E354", {"center": v(-571.5, -348.52) * mm, "radius": 9.53 * mm});
            skLineSegment(sketch, "E355", {"start": v(0, -718.93) * mm, "end": v(0, -144.94) * mm});
            skLineSegment(sketch, "E356", {"start": v(-140.18, -437.42) * mm, "end": v(159.73, -437.42) * mm});
            skCircle(sketch, "E357", {"center": v(-571.5, -532.67) * mm, "radius": 9.53 * mm});
            skLineSegment(sketch, "E358", {"start": v(-8.78, 36.15) * mm, "end": v(-10.3, 44.38) * mm});
            skLineSegment(sketch, "E359", {"start": v(-10.3, 44.38) * mm, "end": v(-15.72, 41.22) * mm});
            skLineSegment(sketch, "E360", {"start": v(-15.72, 41.22) * mm, "end": v(-20.3, 40.58) * mm});
            skLineSegment(sketch, "E361", {"start": v(-20.3, 40.58) * mm, "end": v(-23.87, 41.6) * mm});
            skLineSegment(sketch, "E362", {"start": v(-23.87, 41.6) * mm, "end": v(-24, 45.55) * mm});
            skLineSegment(sketch, "E363", {"start": v(-24, 45.55) * mm, "end": v(-19.42, 46.82) * mm});
            skLineSegment(sketch, "E364", {"start": v(-19.42, 46.82) * mm, "end": v(-14.97, 49.04) * mm});
            skLineSegment(sketch, "E365", {"start": v(-23.04, 57.1) * mm, "end": v(-25.21, 54.93) * mm});
            skLineSegment(sketch, "E366", {"start": v(-25.21, 54.93) * mm, "end": v(-23.16, 53.1) * mm});
            skLineSegment(sketch, "E367", {"start": v(-23.16, 53.1) * mm, "end": v(-18.93, 52.99) * mm});
            skLineSegment(sketch, "E368", {"start": v(33.83, -51.53) * mm, "end": v(35.86, -61.51) * mm});
            skLineSegment(sketch, "E369", {"start": v(35.86, -61.51) * mm, "end": v(41.89, -66.6) * mm});
            skLineSegment(sketch, "E370", {"start": v(41.89, -66.6) * mm, "end": v(33.83, -66.54) * mm});
            skSolve(sketch);
        }
        {
            var Q0;
            {var subQ1=sQuery(id+"F0.wireOp",EDGE,"E0.bottom");var subQ3=sQuery(id+"F0.wireOp",EDGE,"E6.left");var subQ4=makeQuery(id+"F0.imprint","INTERSECT",VERTEX,{"derivedFrom":[subQ1,subQ3]});Q0=makeQuery(id+"F0.imprint","IMPRINT",FACE,{"disambiguationData":[TD([[makeQuery(id+"F0.imprint","IMPRINT",EDGE,{"disambiguationData":[TD([[subQ4,1.0]])],"derivedFrom":subQ1}),1.0]])]});}
            var Q1;
            {var subQ1=sQuery(id+"F0.wireOp",EDGE,"E0.bottom");var subQ3=sQuery(id+"F0.wireOp",EDGE,"E6.right");var subQ4=makeQuery(id+"F0.imprint","INTERSECT",VERTEX,{"derivedFrom":[subQ1,subQ3]});Q1=makeQuery(id+"F0.imprint","IMPRINT",FACE,{"disambiguationData":[TD([[makeQuery(id+"F0.imprint","IMPRINT",EDGE,{"disambiguationData":[TD([[subQ4,-1.0]])],"derivedFrom":subQ1}),1.0]])]});}
            var Q2;
            {var subQ0=sQuery(id+"F0.wireOp",EDGE,"E3");Q2=makeQuery(id+"F0.imprint","IMPRINT",FACE,{"disambiguationData":[TD([[makeQuery(id+"F0.imprint","IMPRINT",EDGE,{"derivedFrom":subQ0}),1.0]])]});}
            var Q3;
            {var subQ0=sQuery(id+"F0.wireOp",EDGE,"0NorEr0o-LK0v-ndRV-EvyM-FVn7yfBQF9nJ");Q3=makeQuery(id+"F0.imprint","IMPRINT",FACE,{"disambiguationData":[TD([[makeQuery(id+"F0.imprint","IMPRINT",EDGE,{"derivedFrom":subQ0}),1.0]])]});}
            var Q4;
            Q4=makeQuery(id+"F0.imprint","IMPRINT",FACE,{"disambiguationData":[TD([[makeQuery(id+"F0.imprint","IMPRINT",EDGE,{"derivedFrom":sQuery(id+"F0.wireOp",EDGE,"E34")}),-1.0]])]});
            var Q5;
            {var subQ3=sQuery(id+"F0.wireOp",EDGE,"CkrFr4Ka-XNqX-OoZ0-1zal-H5uxqjd8LDBE");var subQ5=sQuery(id+"F0.wireOp",EDGE,"kv3bsJPv-IMs3-Gm7j-kYb6-OrEtLbo6LIeh");var subQ6=makeQuery(id+"F0.imprint","INTERSECT",VERTEX,{"derivedFrom":[subQ5,subQ3]});Q5=makeQuery(id+"F0.imprint","IMPRINT",FACE,{"disambiguationData":[TD([[makeQuery(id+"F0.imprint","IMPRINT",EDGE,{"disambiguationData":[TD([[subQ6,-1.0]])],"derivedFrom":subQ5}),1.0]])]});}
            var Q6;
            Q6=makeQuery(id+"F0.imprint","IMPRINT",FACE,{"disambiguationData":[TD([[makeQuery(id+"F0.imprint","IMPRINT",EDGE,{"derivedFrom":sQuery(id+"F0.wireOp",EDGE,"E13")}),-1.0]])]});
            var Q7;
            {var subQ1=sQuery(id+"F0.wireOp",EDGE,"E0.right");var subQ3=sQuery(id+"F0.wireOp",EDGE,"qmvWcmrc-MJxs-LFjd-3G6s-gt8k63rvKK21");var subQ4=makeQuery(id+"F0.imprint","INTERSECT",VERTEX,{"derivedFrom":[subQ1,subQ3]});Q7=makeQuery(id+"F0.imprint","IMPRINT",FACE,{"disambiguationData":[TD([[makeQuery(id+"F0.imprint","IMPRINT",EDGE,{"disambiguationData":[TD([[subQ4,1.0]])],"derivedFrom":subQ1}),1.0]])]});}
            var Q8;
            {var subQ0=sQuery(id+"F0.wireOp",EDGE,"E36");Q8=makeQuery(id+"F0.imprint","IMPRINT",FACE,{"disambiguationData":[TD([[makeQuery(id+"F0.imprint","IMPRINT",EDGE,{"derivedFrom":subQ0}),-1.0]])]});}
            var Q9;
            {var subQ17=sQuery(id+"F0.wireOp",EDGE,"E3");Q9=makeQuery(id+"F0.imprint","IMPRINT",FACE,{"disambiguationData":[TD([[makeQuery(id+"F0.imprint","IMPRINT",EDGE,{"derivedFrom":subQ17}),-1.0]])]});}
            var Q10;
            Q10=makeQuery(id+"F0.imprint","IMPRINT",FACE,{"disambiguationData":[TD([[makeQuery(id+"F0.imprint","IMPRINT",EDGE,{"derivedFrom":sQuery(id+"F0.wireOp",EDGE,"E16")}),1.0]])]});
            var Q11;
            Q11=makeQuery(id+"F0.imprint","IMPRINT",FACE,{"disambiguationData":[TD([[makeQuery(id+"F0.imprint","IMPRINT",EDGE,{"derivedFrom":sQuery(id+"F0.wireOp",EDGE,"E32")}),1.0]])]});
            var Q12;
            Q12=makeQuery(id+"F0.imprint","IMPRINT",FACE,{"disambiguationData":[TD([[makeQuery(id+"F0.imprint","IMPRINT",EDGE,{"derivedFrom":sQuery(id+"F0.wireOp",EDGE,"E30")}),1.0]])]});
            var Q13;
            {var subQ1=sQuery(id+"F0.wireOp",EDGE,"YWdyKWGf-AcJh-LXfP-GXcR-xxzKlvchTPTB");Q13=makeQuery(id+"F0.imprint","IMPRINT",FACE,{"disambiguationData":[TD([[makeQuery(id+"F0.imprint","IMPRINT",EDGE,{"derivedFrom":subQ1}),1.0]])]});}
            var Q14;
            {var subQ1=sQuery(id+"F0.wireOp",EDGE,"iPMD3h6u-pCTR-AWi5-KNE8-7OXAHdy224GQ");Q14=makeQuery(id+"F0.imprint","IMPRINT",FACE,{"disambiguationData":[TD([[makeQuery(id+"F0.imprint","IMPRINT",EDGE,{"derivedFrom":subQ1}),1.0]])]});}
            var Q15;
            {var subQ1=sQuery(id+"F0.wireOp",EDGE,"4dLwsYxT-3ZgV-CAha-Z0Do-N82PuPM7W6ES");Q15=makeQuery(id+"F0.imprint","IMPRINT",FACE,{"disambiguationData":[TD([[makeQuery(id+"F0.imprint","IMPRINT",EDGE,{"derivedFrom":subQ1}),1.0]])]});}
            var Q16;
            {var subQ1=sQuery(id+"F0.wireOp",EDGE,"E327.bottom");Q16=makeQuery(id+"F0.imprint","IMPRINT",FACE,{"disambiguationData":[TD([[makeQuery(id+"F0.imprint","IMPRINT",EDGE,{"derivedFrom":subQ1}),-1.0]])]});}
            var Q17;
            {var subQ0=sQuery(id+"F0.wireOp",EDGE,"E326");var subQ1=sQuery(id+"F0.wireOp",EDGE,"E323");var subQ2=makeQuery(id+"F0.imprint","INTERSECT",VERTEX,{"derivedFrom":[subQ1,subQ0]});Q17=makeQuery(id+"F0.imprint","IMPRINT",FACE,{"disambiguationData":[TD([[makeQuery(id+"F0.imprint","IMPRINT",EDGE,{"disambiguationData":[TD([[subQ2,-1.0]])],"derivedFrom":subQ1}),-1.0]])]});}
            var Q18;
            {var subQ0=sQuery(id+"F0.wireOp",EDGE,"E327.right");var subQ1=sQuery(id+"F0.wireOp",EDGE,"E323");var subQ2=makeQuery(id+"F0.imprint","INTERSECT",VERTEX,{"derivedFrom":[subQ1,subQ0]});Q18=makeQuery(id+"F0.imprint","IMPRINT",FACE,{"disambiguationData":[TD([[makeQuery(id+"F0.imprint","IMPRINT",EDGE,{"disambiguationData":[TD([[subQ2,-1.0]])],"derivedFrom":subQ1}),1.0]])]});}
            var Q19;
            {var subQ5=sQuery(id+"F0.wireOp",EDGE,"E328");var subQ6=sQuery(id+"F0.wireOp",EDGE,"E327.left");var subQ7=makeQuery(id+"F0.imprint","INTERSECT",VERTEX,{"derivedFrom":[subQ6,subQ5]});Q19=makeQuery(id+"F0.imprint","IMPRINT",FACE,{"disambiguationData":[TD([[makeQuery(id+"F0.imprint","IMPRINT",EDGE,{"disambiguationData":[TD([[subQ7,-1.0]])],"derivedFrom":subQ6}),1.0]])]});}
            var Q20;
            {var subQ0=sQuery(id+"F0.wireOp",EDGE,"E328");var subQ1=sQuery(id+"F0.wireOp",EDGE,"E327.right");var subQ2=makeQuery(id+"F0.imprint","INTERSECT",VERTEX,{"derivedFrom":[subQ1,subQ0]});Q20=makeQuery(id+"F0.imprint","IMPRINT",FACE,{"disambiguationData":[TD([[makeQuery(id+"F0.imprint","IMPRINT",EDGE,{"disambiguationData":[TD([[subQ2,-1.0]])],"derivedFrom":subQ1}),-1.0]])]});}
            var Q21;
            {var subQ0=sQuery(id+"F0.wireOp",EDGE,"E331");var subQ1=sQuery(id+"F0.wireOp",EDGE,"E327.left");var subQ2=makeQuery(id+"F0.imprint","INTERSECT",VERTEX,{"derivedFrom":[subQ1,subQ0]});Q21=makeQuery(id+"F0.imprint","IMPRINT",FACE,{"disambiguationData":[TD([[makeQuery(id+"F0.imprint","IMPRINT",EDGE,{"disambiguationData":[TD([[subQ2,-1.0]])],"derivedFrom":subQ1}),1.0]])]});}
            var Q22;
            {var subQ1=sQuery(id+"F0.wireOp",EDGE,"E326");var subQ6=sQuery(id+"F0.wireOp",EDGE,"E323");var subQ10=makeQuery(id+"F0.imprint","INTERSECT",VERTEX,{"derivedFrom":[subQ6,subQ1]});Q22=makeQuery(id+"F0.imprint","IMPRINT",FACE,{"disambiguationData":[TD([[makeQuery(id+"F0.imprint","IMPRINT",EDGE,{"disambiguationData":[TD([[subQ10,-1.0]])],"derivedFrom":subQ6}),1.0]])]});}
            var Q23;
            {var subQ0=sQuery(id+"F0.wireOp",EDGE,"E328");var subQ1=sQuery(id+"F0.wireOp",EDGE,"E5.right");var subQ2=makeQuery(id+"F0.imprint","INTERSECT",VERTEX,{"derivedFrom":[subQ1,subQ0]});Q23=makeQuery(id+"F0.imprint","IMPRINT",FACE,{"disambiguationData":[TD([[makeQuery(id+"F0.imprint","IMPRINT",EDGE,{"disambiguationData":[TD([[subQ2,-1.0]])],"derivedFrom":subQ1}),-1.0]])]});}
            var Q24;
            {var subQ0=sQuery(id+"F0.wireOp",EDGE,"E331");var subQ1=sQuery(id+"F0.wireOp",EDGE,"E5.right");var subQ2=makeQuery(id+"F0.imprint","INTERSECT",VERTEX,{"derivedFrom":[subQ1,subQ0]});Q24=makeQuery(id+"F0.imprint","IMPRINT",FACE,{"disambiguationData":[TD([[makeQuery(id+"F0.imprint","IMPRINT",EDGE,{"disambiguationData":[TD([[subQ2,-1.0]])],"derivedFrom":subQ1}),-1.0]])]});}
            var Q25;
            {var subQ0=sQuery(id+"F0.wireOp",EDGE,"E329");var subQ1=sQuery(id+"F0.wireOp",EDGE,"E327.right");var subQ2=makeQuery(id+"F0.imprint","INTERSECT",VERTEX,{"derivedFrom":[subQ1,subQ0]});Q25=makeQuery(id+"F0.imprint","IMPRINT",FACE,{"disambiguationData":[TD([[makeQuery(id+"F0.imprint","IMPRINT",EDGE,{"disambiguationData":[TD([[subQ2,-1.0]])],"derivedFrom":subQ1}),-1.0]])]});}
            var Q26;
            {var subQ0=sQuery(id+"F0.wireOp",EDGE,"E330");var subQ1=sQuery(id+"F0.wireOp",EDGE,"E327.left");var subQ2=makeQuery(id+"F0.imprint","INTERSECT",VERTEX,{"derivedFrom":[subQ1,subQ0]});Q26=makeQuery(id+"F0.imprint","IMPRINT",FACE,{"disambiguationData":[TD([[makeQuery(id+"F0.imprint","IMPRINT",EDGE,{"disambiguationData":[TD([[subQ2,-1.0]])],"derivedFrom":subQ1}),1.0]])]});}
            var Q27;
            {var subQ1=sQuery(id+"F0.wireOp",EDGE,"E324");var subQ5=sQuery(id+"F0.wireOp",EDGE,"E325");var subQ6=makeQuery(id+"F0.imprint","INTERSECT",VERTEX,{"derivedFrom":[subQ1,subQ5]});Q27=makeQuery(id+"F0.imprint","IMPRINT",FACE,{"disambiguationData":[TD([[makeQuery(id+"F0.imprint","IMPRINT",EDGE,{"disambiguationData":[TD([[subQ6,-1.0]])],"derivedFrom":subQ1}),1.0]])]});}
            var Q28;
            {var subQ0=sQuery(id+"F0.wireOp",EDGE,"E327.left");var subQ1=sQuery(id+"F0.wireOp",EDGE,"E324");var subQ2=makeQuery(id+"F0.imprint","INTERSECT",VERTEX,{"derivedFrom":[subQ1,subQ0]});Q28=makeQuery(id+"F0.imprint","IMPRINT",FACE,{"disambiguationData":[TD([[makeQuery(id+"F0.imprint","IMPRINT",EDGE,{"disambiguationData":[TD([[subQ2,-1.0]])],"derivedFrom":subQ1}),1.0]])]});}
            var Q29;
            {var subQ0=sQuery(id+"F0.wireOp",EDGE,"E325");var subQ1=sQuery(id+"F0.wireOp",EDGE,"E324");var subQ2=makeQuery(id+"F0.imprint","INTERSECT",VERTEX,{"derivedFrom":[subQ1,subQ0]});Q29=makeQuery(id+"F0.imprint","IMPRINT",FACE,{"disambiguationData":[TD([[makeQuery(id+"F0.imprint","IMPRINT",EDGE,{"disambiguationData":[TD([[subQ2,-1.0]])],"derivedFrom":subQ1}),-1.0]])]});}
            var Q30;
            {var subQ1=sQuery(id+"F0.wireOp",EDGE,"E327.top");Q30=makeQuery(id+"F0.imprint","IMPRINT",FACE,{"disambiguationData":[TD([[makeQuery(id+"F0.imprint","IMPRINT",EDGE,{"derivedFrom":subQ1}),1.0]])]});}
            var Q31;
            {var subQ0=sQuery(id+"F0.wireOp",EDGE,"E331");var subQ1=sQuery(id+"F0.wireOp",EDGE,"E5.right");var subQ2=makeQuery(id+"F0.imprint","INTERSECT",VERTEX,{"derivedFrom":[subQ1,subQ0]});Q31=makeQuery(id+"F0.imprint","IMPRINT",FACE,{"disambiguationData":[TD([[makeQuery(id+"F0.imprint","IMPRINT",EDGE,{"disambiguationData":[TD([[subQ2,-1.0]])],"derivedFrom":subQ1}),1.0]])]});}
            var Q32;
            {var subQ5=sQuery(id+"F0.wireOp",EDGE,"E328");var subQ8=sQuery(id+"F0.wireOp",EDGE,"E5.right");var subQ9=makeQuery(id+"F0.imprint","INTERSECT",VERTEX,{"derivedFrom":[subQ8,subQ5]});Q32=makeQuery(id+"F0.imprint","IMPRINT",FACE,{"disambiguationData":[TD([[makeQuery(id+"F0.imprint","IMPRINT",EDGE,{"disambiguationData":[TD([[subQ9,-1.0]])],"derivedFrom":subQ8}),1.0]])]});}
            var Q33;
            {var subQ0=sQuery(id+"F0.wireOp",EDGE,"E328");var subQ1=sQuery(id+"F0.wireOp",EDGE,"E326");var subQ2=makeQuery(id+"F0.imprint","INTERSECT",VERTEX,{"derivedFrom":[subQ1,subQ0]});Q33=makeQuery(id+"F0.imprint","IMPRINT",FACE,{"disambiguationData":[TD([[makeQuery(id+"F0.imprint","IMPRINT",EDGE,{"disambiguationData":[TD([[subQ2,-1.0]])],"derivedFrom":subQ1}),1.0]])]});}
            var Q34;
            {var subQ0=sQuery(id+"F0.wireOp",EDGE,"E329");var subQ1=sQuery(id+"F0.wireOp",EDGE,"E5.right");var subQ2=makeQuery(id+"F0.imprint","INTERSECT",VERTEX,{"derivedFrom":[subQ1,subQ0]});Q34=makeQuery(id+"F0.imprint","IMPRINT",FACE,{"disambiguationData":[TD([[makeQuery(id+"F0.imprint","IMPRINT",EDGE,{"disambiguationData":[TD([[subQ2,-1.0]])],"derivedFrom":subQ1}),-1.0]])]});}
            var Q35;
            {var subQ3=sQuery(id+"F0.wireOp",EDGE,"E5.right");var subQ7=sQuery(id+"F0.wireOp",EDGE,"E329");var subQ9=makeQuery(id+"F0.imprint","INTERSECT",VERTEX,{"derivedFrom":[subQ3,subQ7]});Q35=makeQuery(id+"F0.imprint","IMPRINT",FACE,{"disambiguationData":[TD([[makeQuery(id+"F0.imprint","IMPRINT",EDGE,{"disambiguationData":[TD([[subQ9,-1.0]])],"derivedFrom":subQ3}),1.0]])]});}
            var Q36;
            {var subQ0=sQuery(id+"F0.wireOp",EDGE,"E331");var subQ1=sQuery(id+"F0.wireOp",EDGE,"E324");var subQ2=makeQuery(id+"F0.imprint","INTERSECT",VERTEX,{"derivedFrom":[subQ1,subQ0]});Q36=makeQuery(id+"F0.imprint","IMPRINT",FACE,{"disambiguationData":[TD([[makeQuery(id+"F0.imprint","IMPRINT",EDGE,{"disambiguationData":[TD([[subQ2,1.0]])],"derivedFrom":subQ1}),-1.0]])]});}
            var Q37;
            {var subQ0=sQuery(id+"F0.wireOp",EDGE,"E328");var subQ1=sQuery(id+"F0.wireOp",EDGE,"E5.left");var subQ2=makeQuery(id+"F0.imprint","INTERSECT",VERTEX,{"derivedFrom":[subQ1,subQ0]});Q37=makeQuery(id+"F0.imprint","IMPRINT",FACE,{"disambiguationData":[TD([[makeQuery(id+"F0.imprint","IMPRINT",EDGE,{"disambiguationData":[TD([[subQ2,-1.0]])],"derivedFrom":subQ1}),1.0]])]});}
            var Q38;
            {var subQ0=sQuery(id+"F0.wireOp",EDGE,"E330");var subQ1=sQuery(id+"F0.wireOp",EDGE,"E5.left");var subQ2=makeQuery(id+"F0.imprint","INTERSECT",VERTEX,{"derivedFrom":[subQ1,subQ0]});Q38=makeQuery(id+"F0.imprint","IMPRINT",FACE,{"disambiguationData":[TD([[makeQuery(id+"F0.imprint","IMPRINT",EDGE,{"disambiguationData":[TD([[subQ2,-1.0]])],"derivedFrom":subQ1}),1.0]])]});}
            var Q39;
            {var subQ0=sQuery(id+"F0.wireOp",EDGE,"E331");var subQ1=sQuery(id+"F0.wireOp",EDGE,"E5.left");var subQ2=makeQuery(id+"F0.imprint","INTERSECT",VERTEX,{"derivedFrom":[subQ1,subQ0]});Q39=makeQuery(id+"F0.imprint","IMPRINT",FACE,{"disambiguationData":[TD([[makeQuery(id+"F0.imprint","IMPRINT",EDGE,{"disambiguationData":[TD([[subQ2,-1.0]])],"derivedFrom":subQ1}),1.0]])]});}
            var Q40;
            {var subQ3=sQuery(id+"F0.wireOp",EDGE,"E5.left");var subQ5=sQuery(id+"F0.wireOp",EDGE,"E331");var subQ8=makeQuery(id+"F0.imprint","INTERSECT",VERTEX,{"derivedFrom":[subQ3,subQ5]});Q40=makeQuery(id+"F0.imprint","IMPRINT",FACE,{"disambiguationData":[TD([[makeQuery(id+"F0.imprint","IMPRINT",EDGE,{"disambiguationData":[TD([[subQ8,-1.0]])],"derivedFrom":subQ3}),-1.0]])]});}
            var Q41;
            {var subQ0=sQuery(id+"F0.wireOp",EDGE,"E328");var subQ1=sQuery(id+"F0.wireOp",EDGE,"E5.left");var subQ2=makeQuery(id+"F0.imprint","INTERSECT",VERTEX,{"derivedFrom":[subQ1,subQ0]});Q41=makeQuery(id+"F0.imprint","IMPRINT",FACE,{"disambiguationData":[TD([[makeQuery(id+"F0.imprint","IMPRINT",EDGE,{"disambiguationData":[TD([[subQ2,-1.0]])],"derivedFrom":subQ1}),-1.0]])]});}
            var Q42;
            {var subQ3=sQuery(id+"F0.wireOp",EDGE,"E330");var subQ7=sQuery(id+"F0.wireOp",EDGE,"E5.left");var subQ9=makeQuery(id+"F0.imprint","INTERSECT",VERTEX,{"derivedFrom":[subQ7,subQ3]});Q42=makeQuery(id+"F0.imprint","IMPRINT",FACE,{"disambiguationData":[TD([[makeQuery(id+"F0.imprint","IMPRINT",EDGE,{"disambiguationData":[TD([[subQ9,-1.0]])],"derivedFrom":subQ7}),-1.0]])]});}
            var Q43;
            {var subQ5=sQuery(id+"F0.wireOp",EDGE,"E332");Q43=makeQuery(id+"F0.imprint","IMPRINT",FACE,{"disambiguationData":[TD([[makeQuery(id+"F0.imprint","IMPRINT",EDGE,{"derivedFrom":subQ5}),1.0]])]});}
            var Q44;
            {var subQ5=sQuery(id+"F0.wireOp",EDGE,"nelsg07c-jdhX-oppF-J7CI-pHA4MZNmZiMS");Q44=makeQuery(id+"F0.imprint","IMPRINT",FACE,{"disambiguationData":[TD([[makeQuery(id+"F0.imprint","IMPRINT",EDGE,{"derivedFrom":subQ5}),-1.0]])]});}
            var Q45;
            {var subQ3=sQuery(id+"F0.wireOp",EDGE,"E335");Q45=makeQuery(id+"F0.imprint","IMPRINT",FACE,{"disambiguationData":[TD([[makeQuery(id+"F0.imprint","IMPRINT",EDGE,{"derivedFrom":subQ3}),-1.0]])]});}
            var Q46;
            {var subQ5=sQuery(id+"F0.wireOp",EDGE,"E46");var subQ6=sQuery(id+"F0.wireOp",EDGE,"E45");var subQ7=makeQuery(id+"F0.imprint","INTERSECT",VERTEX,{"derivedFrom":[subQ6,subQ5]});Q46=makeQuery(id+"F0.imprint","IMPRINT",FACE,{"disambiguationData":[TD([[makeQuery(id+"F0.imprint","IMPRINT",EDGE,{"disambiguationData":[TD([[subQ7,1.0]])],"derivedFrom":subQ6}),-1.0]])]});}
            var Q47;
            Q47=makeQuery(id+"F0.imprint","IMPRINT",FACE,{"disambiguationData":[TD([[makeQuery(id+"F0.imprint","IMPRINT",EDGE,{"derivedFrom":sQuery(id+"F0.wireOp",EDGE,"E47")}),-1.0]])]});
            var Q48;
            {var subQ0=sQuery(id+"F0.wireOp",EDGE,"E327.right");var subQ9=sQuery(id+"F0.wireOp",EDGE,"E323");var subQ11=makeQuery(id+"F0.imprint","INTERSECT",VERTEX,{"derivedFrom":[subQ9,subQ0]});Q48=makeQuery(id+"F0.imprint","IMPRINT",FACE,{"disambiguationData":[TD([[makeQuery(id+"F0.imprint","IMPRINT",EDGE,{"disambiguationData":[TD([[subQ11,-1.0]])],"derivedFrom":subQ9}),-1.0]])]});}
            var Q49;
            {var subQ0=sQuery(id+"F0.wireOp",EDGE,"E355");var subQ1=sQuery(id+"F0.wireOp",EDGE,"E323");var subQ2=makeQuery(id+"F0.imprint","INTERSECT",VERTEX,{"derivedFrom":[subQ1,subQ0]});Q49=makeQuery(id+"F0.imprint","IMPRINT",FACE,{"disambiguationData":[TD([[makeQuery(id+"F0.imprint","IMPRINT",EDGE,{"disambiguationData":[TD([[subQ2,-1.0]])],"derivedFrom":subQ1}),-1.0]])]});}
            var Q50;
            {var subQ0=sQuery(id+"F0.wireOp",EDGE,"E355");var subQ1=sQuery(id+"F0.wireOp",EDGE,"E323");var subQ2=makeQuery(id+"F0.imprint","INTERSECT",VERTEX,{"derivedFrom":[subQ1,subQ0]});Q50=makeQuery(id+"F0.imprint","IMPRINT",FACE,{"disambiguationData":[TD([[makeQuery(id+"F0.imprint","IMPRINT",EDGE,{"disambiguationData":[TD([[subQ2,-1.0]])],"derivedFrom":subQ1}),1.0]])]});}
            var Q51;
            {var subQ3=sQuery(id+"F0.wireOp",EDGE,"E356");var subQ6=sQuery(id+"F0.wireOp",EDGE,"E327.right");var subQ9=makeQuery(id+"F0.imprint","INTERSECT",VERTEX,{"derivedFrom":[subQ6,subQ3]});Q51=makeQuery(id+"F0.imprint","IMPRINT",FACE,{"disambiguationData":[TD([[makeQuery(id+"F0.imprint","IMPRINT",EDGE,{"disambiguationData":[TD([[subQ9,1.0]])],"derivedFrom":subQ6}),-1.0]])]});}
            var Q52;
            {var subQ0=sQuery(id+"F0.wireOp",EDGE,"E356");var subQ1=sQuery(id+"F0.wireOp",EDGE,"E327.left");var subQ2=makeQuery(id+"F0.imprint","INTERSECT",VERTEX,{"derivedFrom":[subQ1,subQ0]});Q52=makeQuery(id+"F0.imprint","IMPRINT",FACE,{"disambiguationData":[TD([[makeQuery(id+"F0.imprint","IMPRINT",EDGE,{"disambiguationData":[TD([[subQ2,-1.0]])],"derivedFrom":subQ1}),1.0]])]});}
            var Q53;
            {var subQ3=sQuery(id+"F0.wireOp",EDGE,"E356");var subQ7=sQuery(id+"F0.wireOp",EDGE,"E327.right");var subQ9=makeQuery(id+"F0.imprint","INTERSECT",VERTEX,{"derivedFrom":[subQ7,subQ3]});Q53=makeQuery(id+"F0.imprint","IMPRINT",FACE,{"disambiguationData":[TD([[makeQuery(id+"F0.imprint","IMPRINT",EDGE,{"disambiguationData":[TD([[subQ9,-1.0]])],"derivedFrom":subQ7}),-1.0]])]});}
            var Q54;
            {var subQ0=sQuery(id+"F0.wireOp",EDGE,"E355");var subQ1=sQuery(id+"F0.wireOp",EDGE,"E325");var subQ2=makeQuery(id+"F0.imprint","INTERSECT",VERTEX,{"derivedFrom":[subQ1,subQ0]});Q54=makeQuery(id+"F0.imprint","IMPRINT",FACE,{"disambiguationData":[TD([[makeQuery(id+"F0.imprint","IMPRINT",EDGE,{"disambiguationData":[TD([[subQ2,-1.0]])],"derivedFrom":subQ1}),-1.0]])]});}
            var Q55;
            {var subQ5=sQuery(id+"F0.wireOp",EDGE,"E355");var subQ10=sQuery(id+"F0.wireOp",EDGE,"E324");var subQ11=makeQuery(id+"F0.imprint","INTERSECT",VERTEX,{"derivedFrom":[subQ10,subQ5]});Q55=makeQuery(id+"F0.imprint","IMPRINT",FACE,{"disambiguationData":[TD([[makeQuery(id+"F0.imprint","IMPRINT",EDGE,{"disambiguationData":[TD([[subQ11,-1.0]])],"derivedFrom":subQ10}),-1.0]])]});}
            var Q56;
            {var subQ0=sQuery(id+"F0.wireOp",EDGE,"E331");var subQ1=sQuery(id+"F0.wireOp",EDGE,"E328");var subQ2=makeQuery(id+"F0.imprint","INTERSECT",VERTEX,{"derivedFrom":[subQ1,subQ0]});Q56=makeQuery(id+"F0.imprint","IMPRINT",FACE,{"disambiguationData":[TD([[makeQuery(id+"F0.imprint","IMPRINT",EDGE,{"disambiguationData":[TD([[subQ2,-1.0]])],"derivedFrom":subQ1}),-1.0]])]});}
            var Q57;
            {var subQ0=sQuery(id+"F0.wireOp",EDGE,"E355");var subQ1=sQuery(id+"F0.wireOp",EDGE,"E329");var subQ2=makeQuery(id+"F0.imprint","INTERSECT",VERTEX,{"derivedFrom":[subQ1,subQ0]});Q57=makeQuery(id+"F0.imprint","IMPRINT",FACE,{"disambiguationData":[TD([[makeQuery(id+"F0.imprint","IMPRINT",EDGE,{"disambiguationData":[TD([[subQ2,-1.0]])],"derivedFrom":subQ1}),1.0]])]});}
            var Q58;
            {var subQ0=sQuery(id+"F0.wireOp",EDGE,"E355");var subQ1=sQuery(id+"F0.wireOp",EDGE,"E324");var subQ2=makeQuery(id+"F0.imprint","INTERSECT",VERTEX,{"derivedFrom":[subQ1,subQ0]});Q58=makeQuery(id+"F0.imprint","IMPRINT",FACE,{"disambiguationData":[TD([[makeQuery(id+"F0.imprint","IMPRINT",EDGE,{"disambiguationData":[TD([[subQ2,-1.0]])],"derivedFrom":subQ1}),1.0]])]});}
            extrude(context, id + "F1", {"entities" : qUnion([Q0, Q1, Q2, Q3, Q4, Q5, Q6, Q7, Q8, Q9, Q10, Q11, Q12, Q13, Q14, Q15, Q16, Q17, Q18, Q19, Q20, Q21, Q22, Q23, Q24, Q25, Q26, Q27, Q28, Q29, Q30, Q31, Q32, Q33, Q34, Q35, Q36, Q37, Q38, Q39, Q40, Q41, Q42, Q43, Q44, Q45, Q46, Q47, Q48, Q49, Q50, Q51, Q52, Q53, Q54, Q55, Q56, Q57, Q58]), "endBound" : BoundingType.SYMMETRIC, "depth" : 6.35 * mm, "offsetDistance" : 25.4 * mm});
        }
        {
            var Q0;
            {var subQ0=sQuery(id+"F0.wireOp",EDGE,"E17");Q0=makeQuery(id+"F0.imprint","IMPRINT",FACE,{"disambiguationData":[TD([[makeQuery(id+"F0.imprint","IMPRINT",EDGE,{"derivedFrom":subQ0}),-1.0]])]});}
            var Q1;
            {var subQ0=sQuery(id+"F0.wireOp",EDGE,"E23");Q1=makeQuery(id+"F0.imprint","IMPRINT",FACE,{"disambiguationData":[TD([[makeQuery(id+"F0.imprint","IMPRINT",EDGE,{"derivedFrom":subQ0}),-1.0]])]});}
            extrude(context, id + "F2", {"entities" : qUnion([Q0, Q1]), "operationType" : NewBodyOperationType.ADD, "oppositeDirection" : true, "depth" : 88.9 * mm});
        }
        {
            var Q0;
            {var subQ0=sQuery(id+"F0.wireOp",EDGE,"E26");Q0=makeQuery(id+"F0.imprint","IMPRINT",FACE,{"disambiguationData":[TD([[makeQuery(id+"F0.imprint","IMPRINT",EDGE,{"derivedFrom":subQ0}),1.0]])]});}
            extrude(context, id + "F3", {"entities" : qUnion([Q0]), "operationType" : NewBodyOperationType.ADD, "depth" : 88.9 * mm});
        }
    });
